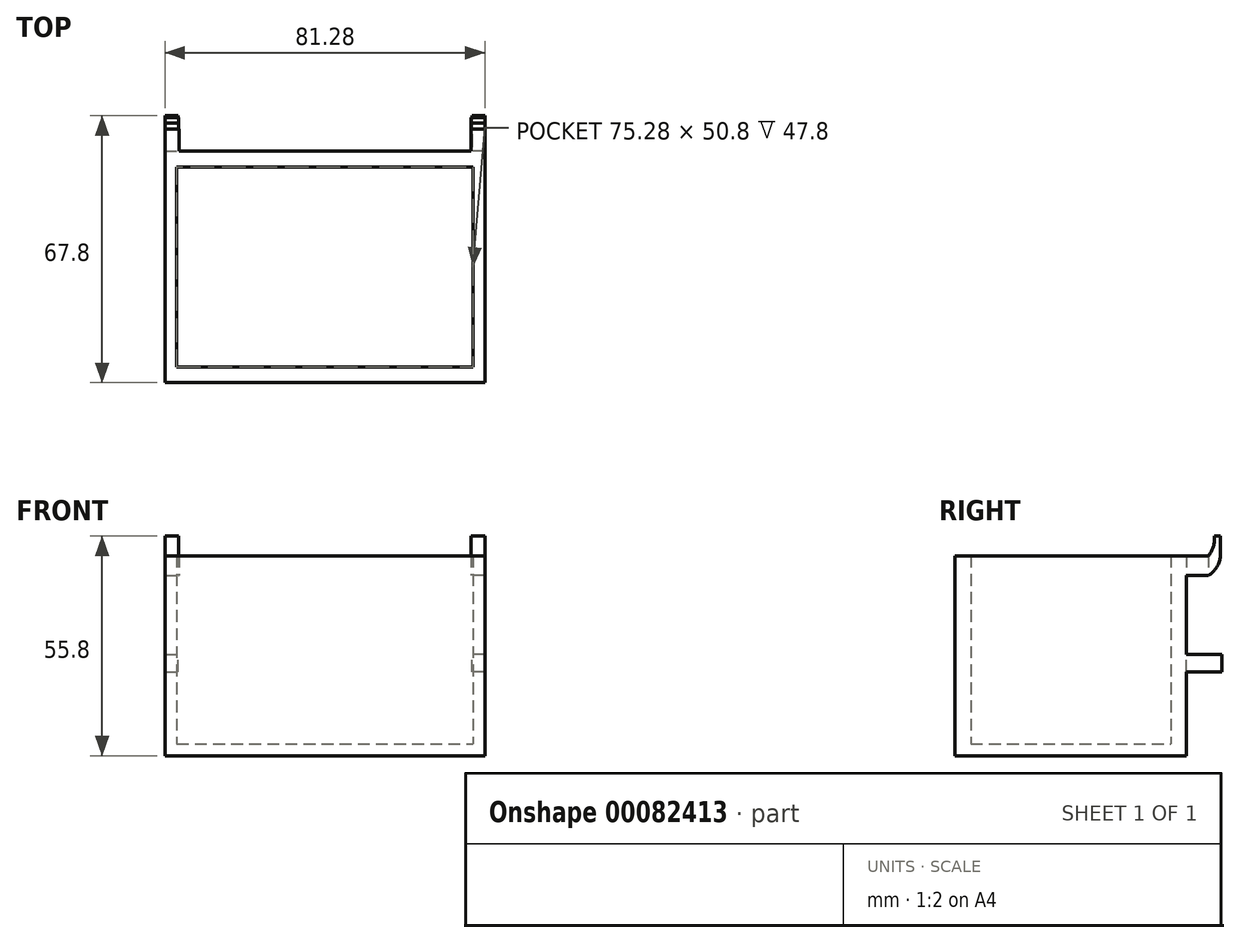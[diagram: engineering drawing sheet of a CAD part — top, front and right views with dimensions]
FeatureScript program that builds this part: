
annotation { "Feature Type Name" : "Feature", "Feature Type Description" : "" }
export const myFeature = defineFeature(function(context is Context, id is Id, definition is map)
    precondition{}
    {
        {
            var Q0;
            Q0=qCreatedBy(makeId("Front.planeOp"),FACE);
            var sketch = newSketch(context, id + "F0", { "sketchPlane" : qUnion([Q0])});
            skLineSegment(sketch, "E0.bottom", {"start": v(40.64, 25.4) * mm, "end": v(-40.64, 25.4) * mm});
            skLineSegment(sketch, "E0.top", {"start": v(40.64, -25.4) * mm, "end": v(-40.64, -25.4) * mm});
            skLineSegment(sketch, "E0.left", {"start": v(40.64, 25.4) * mm, "end": v(40.64, -25.4) * mm});
            skLineSegment(sketch, "E0.right", {"start": v(-40.64, 25.4) * mm, "end": v(-40.64, -25.4) * mm});
            skPoint(sketch, "E0.middle", {"position": v(0, 0) * mm});
            skSolve(sketch);
        }
        {
            var Q0;
            Q0=makeQuery(id+"F0.imprint","IMPRINT",FACE,{"disambiguationData":[TD([[makeQuery(id+"F0.imprint","IMPRINT",EDGE,{"derivedFrom":sQuery(id+"F0.wireOp",EDGE,"E0.bottom")}),1.0]])]});
            extrude(context, id + "F1", {"entities" : qUnion([Q0]), "depth" : 4 * mm});
        }
        {
            var Q0;
            Q0=makeQuery(id+"F1.opExtrude","CAP_FACE",FACE,{"disambiguationData":[OSD([sQuery(id+"F0.wireOp",EDGE,"E0.bottom"),sQuery(id+"F0.wireOp",EDGE,"E0.top"),sQuery(id+"F0.wireOp",EDGE,"E0.left"),sQuery(id+"F0.wireOp",EDGE,"E0.right")])],"isStart":false});
            var sketch = newSketch(context, id + "F2", { "sketchPlane" : qUnion([Q0])});
            skLineSegment(sketch, "E1", {"start": v(40.64, 25.4) * mm, "end": v(37.64, 25.4) * mm});
            skLineSegment(sketch, "E2", {"start": v(37.64, 25.4) * mm, "end": v(37.64, -25.4) * mm});
            skLineSegment(sketch, "E3", {"start": v(-40.64, 25.4) * mm, "end": v(-37.64, 25.4) * mm});
            skLineSegment(sketch, "E4", {"start": v(-37.64, 25.4) * mm, "end": v(-37.64, -25.4) * mm});
            skLineSegment(sketch, "E5", {"start": v(-40.64, -25.4) * mm, "end": v(-40.64, -22.4) * mm});
            skLineSegment(sketch, "E6", {"start": v(-40.64, -22.4) * mm, "end": v(40.64, -22.4) * mm});
            skSolve(sketch);
        }
        {
            var Q0;
            {var subQ0=sQuery(id+"F2.wireOp",EDGE,"E3");Q0=makeQuery(id+"F2.imprint","IMPRINT",FACE,{"disambiguationData":[TD([[makeQuery(id+"F2.imprint","IMPRINT",EDGE,{"derivedFrom":subQ0}),1.0]])]});}
            var Q1;
            {var subQ5=sQuery(id+"F2.wireOp",EDGE,"E5");Q1=makeQuery(id+"F2.imprint","IMPRINT",FACE,{"disambiguationData":[TD([[makeQuery(id+"F2.imprint","IMPRINT",EDGE,{"derivedFrom":subQ5}),1.0]])]});}
            var Q2;
            {var subQ0=sQuery(id+"F2.wireOp",EDGE,"E2");var subQ1=makeQuery(id+"F1.opExtrude","CAP_EDGE",EDGE,{"disambiguationData":[OSD([sQuery(id+"F0.wireOp",EDGE,"E0.top")])],"isStart":false});var subQ2=makeQuery(id+"F2.imprint","INTERSECT",VERTEX,{"derivedFrom":[subQ1,subQ0]});Q2=makeQuery(id+"F2.imprint","IMPRINT",FACE,{"disambiguationData":[TD([[makeQuery(id+"F2.imprint","IMPRINT",EDGE,{"disambiguationData":[TD([[subQ2,1.0]])],"derivedFrom":subQ0}),-1.0]])]});}
            var Q3;
            {var subQ0=sQuery(id+"F2.wireOp",EDGE,"E2");var subQ1=makeQuery(id+"F1.opExtrude","CAP_EDGE",EDGE,{"disambiguationData":[OSD([sQuery(id+"F0.wireOp",EDGE,"E0.top")])],"isStart":false});var subQ2=makeQuery(id+"F2.imprint","INTERSECT",VERTEX,{"derivedFrom":[subQ1,subQ0]});Q3=makeQuery(id+"F2.imprint","IMPRINT",FACE,{"disambiguationData":[TD([[makeQuery(id+"F2.imprint","IMPRINT",EDGE,{"disambiguationData":[TD([[subQ2,1.0]])],"derivedFrom":subQ0}),1.0]])]});}
            var Q4;
            {var subQ0=sQuery(id+"F2.wireOp",EDGE,"E1");Q4=makeQuery(id+"F2.imprint","IMPRINT",FACE,{"disambiguationData":[TD([[makeQuery(id+"F2.imprint","IMPRINT",EDGE,{"derivedFrom":subQ0}),1.0]])]});}
            extrude(context, id + "F3", {"entities" : qUnion([Q0, Q1, Q2, Q3, Q4]), "operationType" : NewBodyOperationType.ADD, "depth" : 50.8 * mm});
        }
        {
            var Q0;
            Q0=makeQuery(id+"F3.opExtrude","CAP_FACE",FACE,{"disambiguationData":[OSD([sQuery(id+"F0.wireOp",EDGE,"E0.top"),sQuery(id+"F0.wireOp",EDGE,"E0.left"),sQuery(id+"F0.wireOp",EDGE,"E0.right"),sQuery(id+"F2.wireOp",EDGE,"E1"),sQuery(id+"F2.wireOp",EDGE,"E2"),sQuery(id+"F2.wireOp",EDGE,"E3"),sQuery(id+"F2.wireOp",EDGE,"E4"),sQuery(id+"F2.wireOp",EDGE,"E5"),sQuery(id+"F2.wireOp",EDGE,"E6")])],"isStart":false});
            var sketch = newSketch(context, id + "F4", { "sketchPlane" : qUnion([Q0])});
            skLineSegment(sketch, "E7.bottom", {"start": v(-40.64, -25.4) * mm, "end": v(40.64, -25.4) * mm});
            skLineSegment(sketch, "E7.top", {"start": v(-40.64, 25.4) * mm, "end": v(40.64, 25.4) * mm});
            skLineSegment(sketch, "E7.left", {"start": v(-40.64, -25.4) * mm, "end": v(-40.64, 25.4) * mm});
            skLineSegment(sketch, "E7.right", {"start": v(40.64, -25.4) * mm, "end": v(40.64, 25.4) * mm});
            skSolve(sketch);
        }
        {
            var Q0;
            Q0=makeQuery(id+"F4.imprint","IMPRINT",FACE,{"disambiguationData":[TD([[makeQuery(id+"F4.imprint","IMPRINT",EDGE,{"derivedFrom":sQuery(id+"F4.wireOp",EDGE,"E7.bottom")}),-1.0]])]});
            var Q1;
            {var subQ1=makeQuery(id+"F3.opExtrude","CAP_EDGE",EDGE,{"disambiguationData":[OSD([sQuery(id+"F2.wireOp",EDGE,"E2")])],"isStart":false});Q1=makeQuery(id+"F4.imprint","IMPRINT",FACE,{"disambiguationData":[TD([[makeQuery(id+"F4.imprint","IMPRINT",EDGE,{"derivedFrom":subQ1}),-1.0]])]});}
            extrude(context, id + "F5", {"entities" : qUnion([Q0, Q1]), "operationType" : NewBodyOperationType.ADD, "depth" : 4 * mm});
        }
        {
            var Q0;
            Q0=makeQuery(id+"F1.opExtrude","CAP_FACE",FACE,{"disambiguationData":[OSD([sQuery(id+"F0.wireOp",EDGE,"E0.bottom"),sQuery(id+"F0.wireOp",EDGE,"E0.top"),sQuery(id+"F0.wireOp",EDGE,"E0.left"),sQuery(id+"F0.wireOp",EDGE,"E0.right")])],"isStart":true});
            var sketch = newSketch(context, id + "F6", { "sketchPlane" : qUnion([Q0])});
            skLineSegment(sketch, "E8.bottom", {"start": v(-40.64, 25.4) * mm, "end": v(-37.04, 25.4) * mm});
            skLineSegment(sketch, "E8.top", {"start": v(-40.64, 20.4) * mm, "end": v(-37.04, 20.4) * mm});
            skLineSegment(sketch, "E8.left", {"start": v(-40.64, 25.4) * mm, "end": v(-40.64, 20.4) * mm});
            skLineSegment(sketch, "E8.right", {"start": v(-37.04, 25.4) * mm, "end": v(-37.04, 20.4) * mm});
            skLineSegment(sketch, "E9.bottom", {"start": v(40.64, 25.4) * mm, "end": v(37.04, 25.4) * mm});
            skLineSegment(sketch, "E9.top", {"start": v(40.64, 20.4) * mm, "end": v(37.04, 20.4) * mm});
            skLineSegment(sketch, "E9.left", {"start": v(40.64, 25.4) * mm, "end": v(40.64, 20.4) * mm});
            skLineSegment(sketch, "E9.right", {"start": v(37.04, 25.4) * mm, "end": v(37.04, 20.4) * mm});
            skSolve(sketch);
        }
        {
            var Q0;
            Q0=makeQuery(id+"F6.imprint","IMPRINT",FACE,{"disambiguationData":[TD([[makeQuery(id+"F6.imprint","IMPRINT",EDGE,{"derivedFrom":sQuery(id+"F6.wireOp",EDGE,"E8.bottom")}),-1.0]])]});
            var Q1;
            Q1=makeQuery(id+"F6.imprint","IMPRINT",FACE,{"disambiguationData":[TD([[makeQuery(id+"F6.imprint","IMPRINT",EDGE,{"derivedFrom":sQuery(id+"F6.wireOp",EDGE,"E9.bottom")}),-1.0]])]});
            extrude(context, id + "F7", {"entities" : qUnion([Q0, Q1]), "operationType" : NewBodyOperationType.ADD, "depth" : 5.6 * mm});
        }
        {
            var Q0;
            {var subQ0=sQuery(id+"F0.wireOp",EDGE,"E0.right");Q0=makeQuery(id+"F7.boolean.opBoolean","MERGE",FACE,{"derivedFrom":[makeQuery(id+"FFt5TNaJEHXHIiC_1.boolean.opBoolean","MERGE",FACE,{"derivedFrom":[makeQuery(id+"F5.boolean.opBoolean","MERGE",FACE,{"derivedFrom":[makeQuery(id+"F3.boolean.opBoolean","MERGE",FACE,{"derivedFrom":[makeQuery(id+"F1.opExtrude","SWEPT_FACE",FACE,{"disambiguationData":[OSD([subQ0])]}),makeQuery(id+"F3.opExtrude","SWEPT_FACE",FACE,{"disambiguationData":[OSD([subQ0,sQuery(id+"F2.wireOp",EDGE,"E5")])]})]}),makeQuery(id+"F5.opExtrude","SWEPT_FACE",FACE,{"disambiguationData":[OSD([sQuery(id+"F4.wireOp",EDGE,"E7.left")])]})]}),makeQuery(id+"FFt5TNaJEHXHIiC_1.opExtrude","SWEPT_FACE",FACE,{"disambiguationData":[OSD([sQuery(id+"FDKxu3rXGsQDrog_1.wireOp",EDGE,"Ldn6VzK0-uFpL-7hFX-0DbD-DI3Ueei5DzqT.left")])]})]}),makeQuery(id+"F7.opExtrude","SWEPT_FACE",FACE,{"disambiguationData":[OSD([sQuery(id+"F6.wireOp",EDGE,"E9.left")])]})]});}
            var sketch = newSketch(context, id + "F8", { "sketchPlane" : qUnion([Q0])});
            skArc(sketch, "E10", {"start": v(-8.6, 25.4) * mm, "mid": v(-7.68, 22.55) * mm, "end": v(-5.6, 20.4) * mm});
            skLineSegment(sketch, "E11", {"start": v(-8.6, 25.4) * mm, "end": v(-8.6, 30.4) * mm});
            skLineSegment(sketch, "E12", {"start": v(-8.6, 30.4) * mm, "end": v(-7.1, 30.4) * mm});
            skArc(sketch, "E13", {"start": v(-7.1, 30.4) * mm, "mid": v(-6.81, 27.76) * mm, "end": v(-5.6, 25.4) * mm});
            skSolve(sketch);
        }
        {
            var Q0;
            Q0=makeQuery(id+"F1.opExtrude","CAP_FACE",FACE,{"disambiguationData":[OSD([sQuery(id+"F0.wireOp",EDGE,"E0.bottom"),sQuery(id+"F0.wireOp",EDGE,"E0.top"),sQuery(id+"F0.wireOp",EDGE,"E0.left"),sQuery(id+"F0.wireOp",EDGE,"E0.right")])],"isStart":true});
            var sketch = newSketch(context, id + "F9", { "sketchPlane" : qUnion([Q0])});
            skLineSegment(sketch, "E14", {"start": v(40.64, 20.4) * mm, "end": v(40.64, 0.4) * mm});
            skLineSegment(sketch, "E15", {"start": v(40.64, 0.4) * mm, "end": v(40.64, -4.1) * mm});
            skLineSegment(sketch, "E16", {"start": v(40.64, -4.1) * mm, "end": v(37.34, -4.1) * mm});
            skLineSegment(sketch, "E17.top", {"start": v(40.64, 0.4) * mm, "end": v(37.34, 0.4) * mm});
            skLineSegment(sketch, "E17.left", {"start": v(40.64, -4.1) * mm, "end": v(40.64, 0.4) * mm});
            skLineSegment(sketch, "E17.right", {"start": v(37.34, -4.1) * mm, "end": v(37.34, 0.4) * mm});
            skLineSegment(sketch, "E18", {"start": v(-40.64, 20.4) * mm, "end": v(-40.64, 0.4) * mm});
            skLineSegment(sketch, "E19", {"start": v(-40.64, 0.4) * mm, "end": v(-37.34, 0.4) * mm});
            skLineSegment(sketch, "E20", {"start": v(-40.64, 0.4) * mm, "end": v(-40.64, -4.1) * mm});
            skLineSegment(sketch, "E21", {"start": v(-40.64, -4.1) * mm, "end": v(-37.34, -4.1) * mm});
            skLineSegment(sketch, "E22", {"start": v(-37.34, -4.1) * mm, "end": v(-37.34, 0.4) * mm});
            skSolve(sketch);
        }
        {
            var Q0;
            Q0=makeQuery(id+"F9.imprint","IMPRINT",FACE,{"disambiguationData":[TD([[makeQuery(id+"F9.imprint","IMPRINT",EDGE,{"derivedFrom":sQuery(id+"F9.wireOp",EDGE,"E16")}),-1.0]])]});
            var Q1;
            Q1=makeQuery(id+"F9.imprint","IMPRINT",FACE,{"disambiguationData":[TD([[makeQuery(id+"F9.imprint","IMPRINT",EDGE,{"derivedFrom":sQuery(id+"F9.wireOp",EDGE,"E19")}),-1.0]])]});
            extrude(context, id + "F10", {"entities" : qUnion([Q0, Q1]), "operationType" : NewBodyOperationType.ADD, "depth" : 9 * mm});
        }
        {
            var Q0;
            Q0=makeQuery(id+"F8.imprint","IMPRINT",FACE,{"disambiguationData":[TD([[makeQuery(id+"F8.imprint","IMPRINT",EDGE,{"derivedFrom":sQuery(id+"F8.wireOp",EDGE,"E10")}),1.0]])]});
            extrude(context, id + "F11", {"entities" : qUnion([Q0]), "oppositeDirection" : true, "depth" : 3.5 * mm});
        }
        {
            var Q0;
            Q0=makeQuery(id+"F11.opExtrude","SWEPT_BODY",BODY,{"disambiguationData":[OSD([sQuery(id+"F6.wireOp",EDGE,"E9.left"),sQuery(id+"F8.wireOp",EDGE,"E10"),sQuery(id+"F8.wireOp",EDGE,"E11"),sQuery(id+"F8.wireOp",EDGE,"E12"),sQuery(id+"F8.wireOp",EDGE,"E13")])]});
            var Q1;
            Q1=qCreatedBy(makeId("Right.planeOp"),FACE);
            mirror(context, id + "F12", {"operationType" : NewBodyOperationType.ADD, "entities" : qUnion([Q0]), "mirrorPlane" : qUnion([Q1])});
        }
    });
